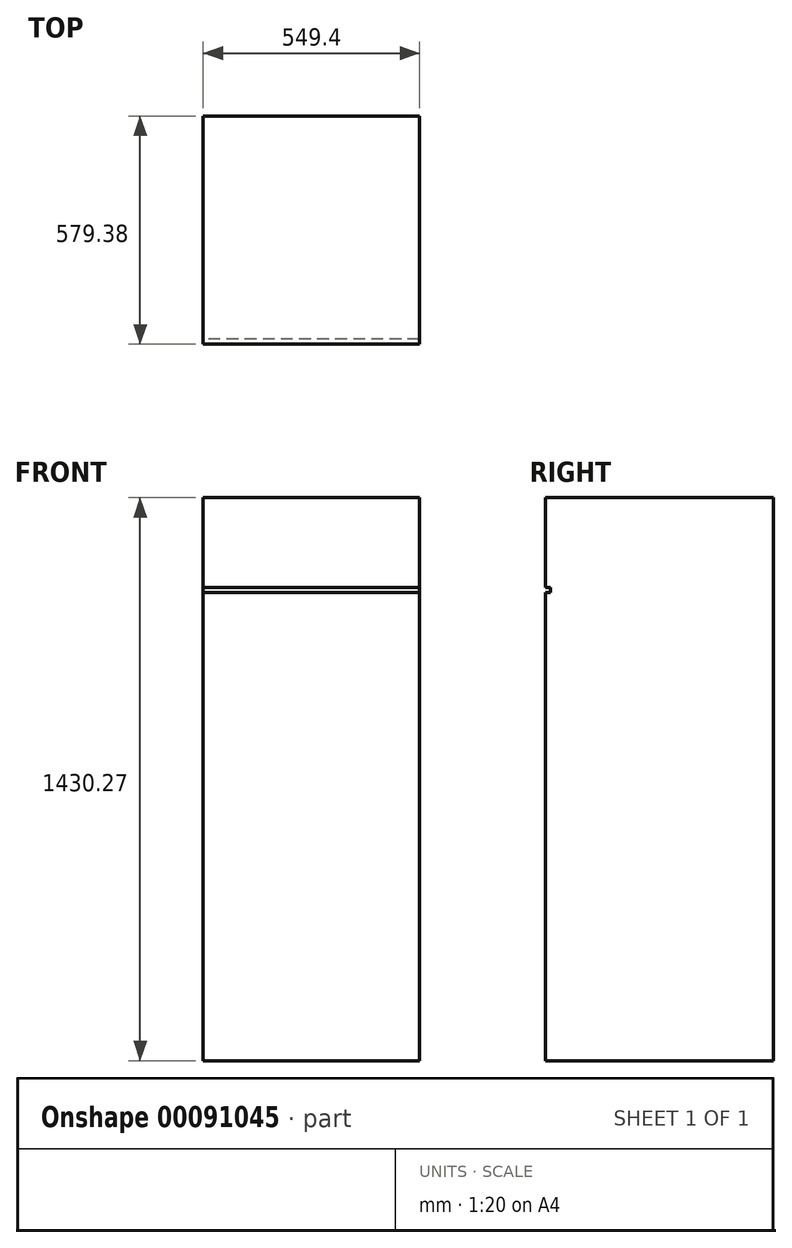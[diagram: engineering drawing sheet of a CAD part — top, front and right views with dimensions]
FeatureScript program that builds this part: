
annotation { "Feature Type Name" : "Feature", "Feature Type Description" : "" }
export const myFeature = defineFeature(function(context is Context, id is Id, definition is map)
    precondition{}
    {
        {
            var Q0;
            Q0=qCreatedBy(makeId("Top.planeOp"),FACE);
            var sketch = newSketch(context, id + "F0", { "sketchPlane" : qUnion([Q0])});
            skLineSegment(sketch, "E0.bottom", {"start": v(-275.09, 300.04) * mm, "end": v(274.31, 300.04) * mm});
            skLineSegment(sketch, "E0.top", {"start": v(-275.09, -279.34) * mm, "end": v(274.31, -279.34) * mm});
            skLineSegment(sketch, "E0.left", {"start": v(-275.09, 300.04) * mm, "end": v(-275.09, -279.34) * mm});
            skLineSegment(sketch, "E0.right", {"start": v(274.31, 300.04) * mm, "end": v(274.31, -279.34) * mm});
            skSolve(sketch);
        }
        {
            var Q0;
            Q0 = qSketchRegion(id + "F0", true);
            extrude(context, id + "F1", {"entities" : qUnion([Q0]), "depth" : 1430.27 * mm});
        }
        {
            var Q0;
            Q0=makeQuery(id+"F1.opExtrude","SWEPT_FACE",FACE,{"disambiguationData":[OSD([sQuery(id+"F0.wireOp",EDGE,"E0.left")])]});
            var sketch = newSketch(context, id + "F2", { "sketchPlane" : qUnion([Q0])});
            skLineSegment(sketch, "E1", {"start": v(279.34, 1201.86) * mm, "end": v(266.64, 1201.86) * mm});
            skLineSegment(sketch, "E2", {"start": v(266.64, 1201.86) * mm, "end": v(266.64, 1189.16) * mm});
            skLineSegment(sketch, "E3", {"start": v(266.64, 1189.16) * mm, "end": v(279.34, 1189.16) * mm});
            skLineSegment(sketch, "E4", {"start": v(279.34, 1189.16) * mm, "end": v(279.34, 1201.86) * mm});
            skPoint(sketch, "E5", {"position": v(279.34, 1195.51) * mm});
            skSolve(sketch);
        }
        {
            var Q0;
            Q0 = qSketchRegion(id + "F2", true);
            extrude(context, id + "F3", {"entities" : qUnion([Q0]), "operationType" : NewBodyOperationType.REMOVE, "endBound" : BoundingType.THROUGH_ALL, "oppositeDirection" : true, "depth" : 25.4 * mm});
        }
    });
